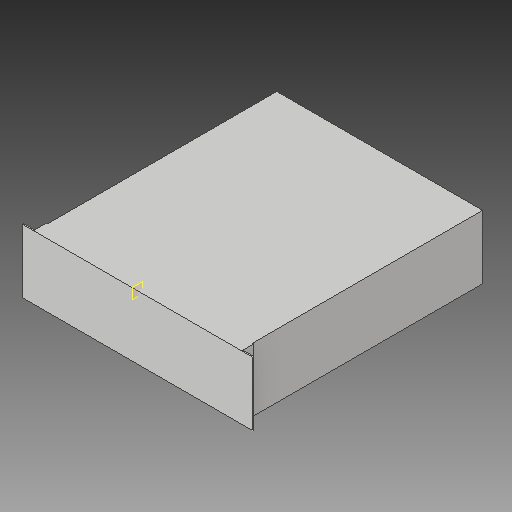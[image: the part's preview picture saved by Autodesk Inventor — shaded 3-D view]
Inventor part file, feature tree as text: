
AUTODESK INVENTOR PART (.ipt)
format: ipt  version: 2017 (Build 210142000, 142)  size: 109,568 bytes
history: native  units: in
note: dims shown in document units (in); Inventor stores cm internally (conversion verified against a paired STEP export)
features: extrude x2, sketch x2, plane x1, mirror x1
ambient origin geometry x8: Origin, YZ Plane, XZ Plane, XY Plane, X Axis, Y Axis, Z Axis, Center Point
bodies: Body1 (feature_tree)
feature tree (6):
  extrude  "Extrusion3"  Depth=20.0in
  plane  "Work Plane3"
  extrude  "Extrusion5"  Depth=1.0in
  mirror  "Mirror1"
  sketch  "Sketch2"  dims[d6=17.0in d7=20.0in]
  sketch  "Sketch4"  dims[d8=5.25in d9=0.0in d13=1.0in d14=1.0in d15=0.104in d16=5.25in d17=0.0in]
